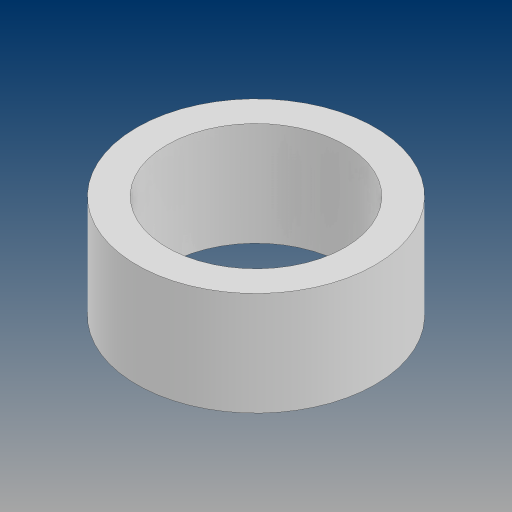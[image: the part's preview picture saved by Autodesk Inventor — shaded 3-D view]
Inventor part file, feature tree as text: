
AUTODESK INVENTOR PART (.ipt)
format: ipt  version: 2024.3 (Build 283343000, 343)  size: 96,768 bytes
history: native  units: in
note: dims shown in document units (in); Inventor stores cm internally (conversion verified against a paired STEP export)
features: extrude x1, sketch x1
ambient origin geometry x8: Origin, YZ Plane, XZ Plane, XY Plane, X Axis, Y Axis, Z Axis, Center Point
bodies: Solid1 (feature_tree)
feature tree (2):
  extrude  "Extrusion1"  Depth=0.326in
  sketch  "Sketch1"  dims[d0=0.56in d1=0.75in d2=0.326in d3=0.0in]
